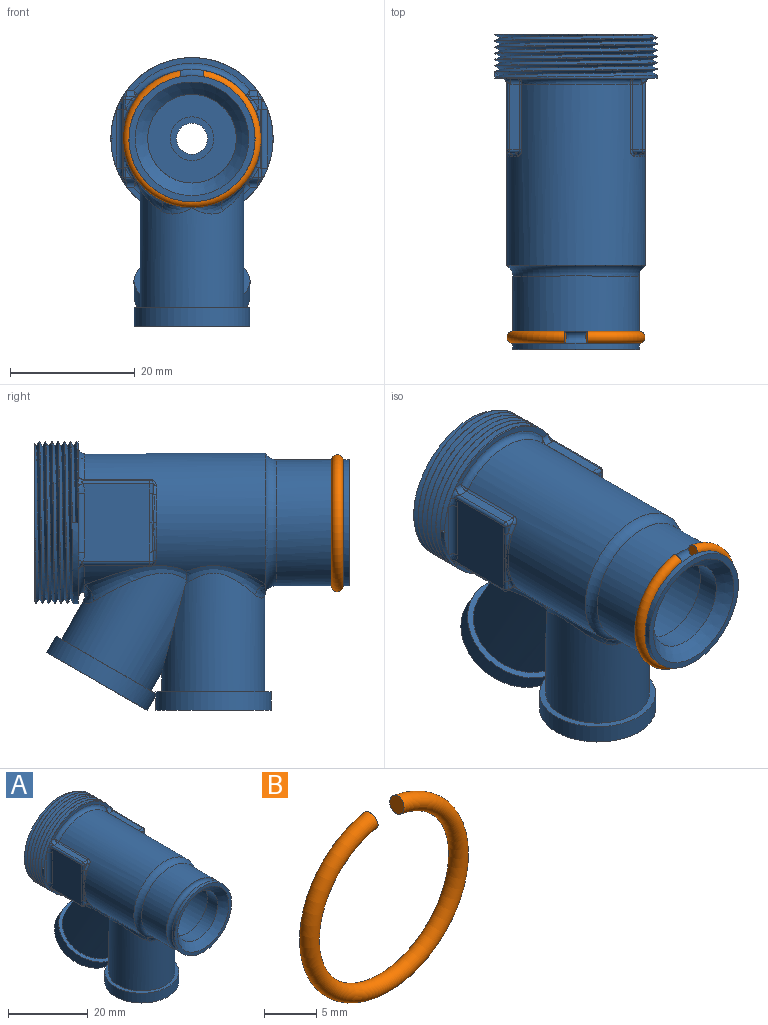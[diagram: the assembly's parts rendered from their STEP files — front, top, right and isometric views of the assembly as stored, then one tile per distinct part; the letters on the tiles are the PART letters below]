
ASSEMBLY  parts=2 mates=1
PART A: 126 faces, bbox 27.1x52x45.9 mm
  f0: cylinder r=10.11mm len=20.22mm, axis (0,1,0), area 60.1mm2, adj f90,f115
  f1: cylinder r=10.11mm len=20.22mm, axis (0,1,0), area 560.4mm2, adj f115,f121
  f2: cylinder r=9.5mm len=20.4mm, axis (0,1,0), area 1205mm2, adj f103,f105,f106
  f3: cylinder r=9.5mm len=22mm, axis (0,1,0), area 1298.6mm2, adj f104,f107,f125
  f4: cylinder r=7.11mm len=14.22mm, axis (0,-1,0), area 160.8mm2, adj f103,f124
  f5: cylinder r=9.3mm len=18.6mm, axis (0,0,-1), area 174.8mm2, adj f92,f93,f99,f101
  f6: cylinder r=11.11mm len=29mm, axis (0,1,0), area 1173.3mm2, adj f29,f30,f31,f34,f36,f42,f44,f45
  f7: plane 20.87x5.25mm, normal (0,-1,0), area 20.2mm2, adj f14,f85,f86,f89
  f8: plane 9.45x0.89mm, normal (0,-1,0), area 5.6mm2, adj f14,f78
  f9: plane 9.45x0.89mm, normal (0,-1,0), area 5.6mm2, adj f14,f77
  f10: plane 1.54x0.83mm, normal (0,-1,0), area 0.6mm2, adj f38,f42,f43
  f11: plane 1.54x0.83mm, normal (0,-1,0), area 0.6mm2, adj f32,f36,f37
  f12: plane 1.54x0.83mm, normal (0,-1,0), area 0.6mm2, adj f58,f62,f65
  f13: plane 20.87x5.25mm, normal (0,-1,0), area 20.2mm2, adj f14,f66,f69,f70
  f14: cylinder r=13mm len=26mm, axis (0,1,0), area 72.4mm2, adj f7,f8,f9,f13,f15,f23,f24,f25
  f15: plane 26.07x26.07mm, normal (0,1,0), area 84.2mm2, adj f14,f23,f24,f125
  f16: plane 10.51x1.54mm, normal (0,0,1), area 16.2mm2, adj f54,f61,f62,f83,f85
  f17: plane 10.51x1.54mm, normal (0,0,1), area 16.2mm2, adj f39,f43,f45,f84,f86
  f18: plane 12.5x10.72mm, normal (-1,0,0), area 131.5mm2, adj f26,f27,f33,f37,f38,f39,f76,f78
  f19: plane 10.51x1.54mm, normal (0,0,-1), area 16.2mm2, adj f31,f32,f33,f70,f72
  f20: plane 10.51x1.54mm, normal (0,0,-1), area 16.2mm2, adj f51,f52,f53,f69,f71
  f21: plane 12.5x10.72mm, normal (1,0,0), area 131.5mm2, adj f48,f49,f51,f54,f58,f59,f75,f77
  f22: plane 1.54x0.83mm, normal (0,-1,0), area 0.6mm2, adj f52,f59,f60
  f23: bspline ~30.02x26mm, area 475.4mm2, adj f14,f15,f24,f25
  f24: bspline ~30.02x26mm, area 508mm2, adj f14,f15,f23,f25
  f25: plane 0.95x0.82mm, normal (0,0,1), area 0.4mm2, adj f14,f23,f24
  f26: bspline ~4.71x0.5mm, area 2mm2, adj f18,f27,f38,f40
  f27: bspline ~4.71x0.5mm, area 2mm2, adj f18,f26,f28,f37
  f28: bspline ~4.71x0.81mm, area 1.5mm2, adj f27,f29,f36,f37
  f29: bspline ~4.54x0.96mm, area 1.7mm2, adj f6,f28,f30,f36
  f30: bspline ~4.54x0.96mm, area 1.7mm2, adj f6,f29,f40,f42
  f31: cylinder r=0.5mm len=10.5mm, axis (0,1,0), area 4.7mm2, adj f6,f19,f34,f68
  f32: cylinder r=0.5mm len=1.54mm, axis (-1,0,0), area 0.9mm2, adj f11,f19,f34,f35
  f33: cylinder r=0.5mm len=10.91mm, axis (0,1,0), area 8.4mm2, adj f18,f19,f35,f74
  f34: bspline ~1.28x1.23mm, area 0.8mm2, adj f6,f31,f32,f36
  f35: sphere r=0.5mm, area 0.4mm2, adj f32,f33,f37
  f36: torus R=11.61mm, axis (0,-1,0), area 1.4mm2, adj f6,f11,f28,f29,f34
  f37: cylinder r=0.5mm len=1.57mm, axis (0,0,1), area 1.2mm2, adj f11,f18,f27,f28,f35
  f38: cylinder r=0.5mm len=1.57mm, axis (0,0,1), area 1.2mm2, adj f10,f18,f26,f40,f41
  f39: cylinder r=0.5mm len=10.91mm, axis (0,1,0), area 8.4mm2, adj f17,f18,f41,f82
  f40: bspline ~4.71x0.81mm, area 1.5mm2, adj f26,f30,f38,f42
  f41: sphere r=0.5mm, area 0.4mm2, adj f38,f39,f43
  f42: torus R=11.61mm, axis (0,-1,0), area 1.4mm2, adj f6,f10,f30,f40,f44
  f43: cylinder r=0.5mm len=1.54mm, axis (1,0,0), area 0.9mm2, adj f10,f17,f41,f44
  f44: bspline ~1.25x1.19mm, area 0.8mm2, adj f6,f42,f43,f45
  f45: cylinder r=0.5mm len=10.5mm, axis (0,1,0), area 4.7mm2, adj f6,f17,f44,f88
  f46: bspline ~4.54x0.96mm, area 1.7mm2, adj f6,f47,f60,f63
  f47: bspline ~4.71x0.81mm, area 1.5mm2, adj f46,f48,f59,f60
  f48: bspline ~4.71x0.5mm, area 2mm2, adj f21,f47,f49,f59
  f49: bspline ~4.71x0.5mm, area 2mm2, adj f21,f48,f50,f58
  f50: bspline ~4.71x0.81mm, area 1.5mm2, adj f49,f58,f63,f65
  f51: cylinder r=0.5mm len=10.91mm, axis (0,1,0), area 8.4mm2, adj f20,f21,f55,f73
  f52: cylinder r=0.5mm len=1.54mm, axis (-1,0,0), area 0.9mm2, adj f20,f22,f55,f56
  f53: cylinder r=0.5mm len=10.5mm, axis (0,1,0), area 4.7mm2, adj f6,f20,f56,f67
  f54: cylinder r=0.5mm len=10.91mm, axis (0,1,0), area 8.4mm2, adj f16,f21,f57,f81
  f55: sphere r=0.5mm, area 0.4mm2, adj f51,f52,f59
  f56: bspline ~1.25x1.19mm, area 0.8mm2, adj f6,f52,f53,f60
  f57: sphere r=0.5mm, area 0.4mm2, adj f54,f58,f62
  f58: cylinder r=0.5mm len=1.57mm, axis (0,0,-1), area 1.2mm2, adj f12,f21,f49,f50,f57
  f59: cylinder r=0.5mm len=1.57mm, axis (0,0,-1), area 1.2mm2, adj f21,f22,f47,f48,f55
  f60: torus R=11.61mm, axis (0,-1,0), area 1.4mm2, adj f6,f22,f46,f47,f56
  f61: cylinder r=0.5mm len=10.5mm, axis (0,1,0), area 4.7mm2, adj f6,f16,f64,f87
  f62: cylinder r=0.5mm len=1.54mm, axis (1,0,0), area 0.9mm2, adj f12,f16,f57,f64
  f63: bspline ~4.54x0.96mm, area 1.7mm2, adj f6,f46,f50,f65
  f64: bspline ~1.28x1.23mm, area 0.8mm2, adj f6,f61,f62,f65
  f65: torus R=11.61mm, axis (0,-1,0), area 1.4mm2, adj f6,f12,f50,f63,f64
  f66: torus R=12.11mm, axis (0,-1,0), area 31.9mm2, adj f6,f13,f67,f68,f118
  f67: bspline ~1.23x1mm, area 0.3mm2, adj f53,f66,f69
  f68: bspline ~1.23x1mm, area 0.3mm2, adj f31,f66,f70
  f69: cylinder r=1mm len=1.37mm, axis (1,0,0), area 2mm2, adj f13,f20,f67,f71
  f70: cylinder r=1mm len=1.37mm, axis (1,0,0), area 2mm2, adj f13,f19,f68,f72
  f71: bspline ~1.11x1.11mm, area 0.2mm2, adj f14,f20,f69,f73
  f72: bspline ~1.14x1.14mm, area 0.2mm2, adj f14,f19,f70,f74
  f73: bspline ~1.89x1.16mm, area 1.1mm2, adj f14,f51,f71,f75
  f74: bspline ~1.82x1.12mm, area 1.1mm2, adj f14,f33,f72,f76
  f75: bspline ~2.1x1.1mm, area 1.8mm2, adj f14,f21,f73,f77
  f76: bspline ~1.52x1mm, area 1.7mm2, adj f14,f18,f74,f78
  f77: cylinder r=1mm len=9.45mm, axis (0,0,1), area 14.8mm2, adj f9,f21,f75,f79
  f78: cylinder r=1mm len=9.45mm, axis (0,0,-1), area 14.8mm2, adj f8,f18,f76,f80
  f79: bspline ~1.52x1mm, area 1.7mm2, adj f14,f21,f77,f81
  f80: bspline ~2.1x1.1mm, area 1.8mm2, adj f14,f18,f78,f82
  f81: bspline ~1.82x1.12mm, area 1.1mm2, adj f14,f54,f79,f83
  f82: bspline ~1.89x1.16mm, area 1.1mm2, adj f14,f39,f80,f84
  f83: bspline ~1.14x1.14mm, area 0.2mm2, adj f14,f16,f81,f85
  f84: bspline ~1.11x1.11mm, area 0.2mm2, adj f14,f17,f82,f86
  f85: cylinder r=1mm len=1.37mm, axis (-1,0,0), area 2mm2, adj f7,f16,f83,f87
  f86: cylinder r=1mm len=1.37mm, axis (-1,0,0), area 2mm2, adj f7,f17,f84,f88
  f87: bspline ~1.23x1mm, area 0.3mm2, adj f61,f85,f89
  f88: bspline ~1.23x1mm, area 0.3mm2, adj f45,f86,f89
  f89: torus R=12.11mm, axis (0,-1,0), area 31.9mm2, adj f6,f7,f87,f88
  f90: plane 20.22x20.22mm, normal (0,-1,0), area 60.4mm2, adj f0,f124
  f91: cylinder r=8.3mm len=18.97mm, axis (0,0,-1), area 744.6mm2, adj f92,f102,f117,f119,f122,f123
  f92: plane 18.6x18.6mm, normal (0,0,1), area 55.3mm2, adj f5,f91
  f93: plane 18.6x18.6mm, normal (0,0,-1), area 183.5mm2, adj f5,f94
  f94: cylinder r=5.3mm len=10.6mm, axis (0,0,-1), area 299.7mm2, adj f93,f95
  f95: plane 10.6x10.6mm, normal (0,0,-1), area 75.7mm2, adj f94,f105
  f96: cone r=5.51mm half-angle=1.8deg, axis (0,-0.5,0.87), area 237.4mm2, adj f97,f100
  f97: cylinder r=5.3mm len=10.95mm, axis (0,0.5,-0.87), area 117.6mm2, adj f96,f98
  f98: plane 18.6x16.11mm, normal (0,0.5,-0.87), area 183.5mm2, adj f97,f101
  f99: plane 18.63x16.06mm, normal (0,-0.5,0.87), area 55mm2, adj f5,f101,f102
  f100: plane 11.03x9.55mm, normal (0,0.5,-0.87), area 82.9mm2, adj f96,f104
  f101: cylinder r=9.3mm len=18.6mm, axis (0,0.5,-0.87), area 174.9mm2, adj f5,f98,f99
  f102: cylinder r=8.3mm len=24.11mm, axis (0,0.5,-0.87), area 581.4mm2, adj f91,f99,f116,f117,f118,f120,f122
  f103: plane 19x19mm, normal (0,1,0), area 124.7mm2, adj f2,f4
  f104: cylinder r=2mm len=9.83mm, axis (0,0.5,-0.87), area 99.1mm2, adj f3,f100
  f105: cylinder r=2mm len=11.59mm, axis (0,0,-1), area 145.6mm2, adj f2,f95
  f106: plane 19x19mm, normal (0,-1,0), area 245mm2, adj f2,f114
  f107: plane 19x19mm, normal (0,1,0), area 219.9mm2, adj f3,f108
  f108: cylinder r=4.5mm len=9mm, axis (0,1,0), area 42.4mm2, adj f107,f109
  f109: plane 9x9mm, normal (0,1,0), area 25.1mm2, adj f108,f110
  f110: cylinder r=3.5mm len=7mm, axis (0,1,0), area 66mm2, adj f109,f111
  f111: plane 7x7mm, normal (0,1,0), area 18.8mm2, adj f110,f112
  f112: cylinder r=2.5mm len=7.54mm, axis (0,1,0), area 118.4mm2, adj f111,f113
  f113: plane 7x7mm, normal (0,-1,0), area 18.8mm2, adj f112,f114
  f114: cylinder r=3.5mm len=7mm, axis (0,1,0), area 55.8mm2, adj f106,f113
  f115: torus R=10.11mm, axis (0,-1,0), area 186.8mm2, adj f0,f1
  f116: bspline ~18.63x6.26mm, area 34.6mm2, adj f6,f102,f117,f118
  f117: bspline ~15.29x5.22mm, area 24.1mm2, adj f6,f91,f102,f116,f119
  f118: bspline ~9.98x3.05mm, area 20.8mm2, adj f66,f102,f116,f120
  f119: bspline ~5.52x2.44mm, area 4.2mm2, adj f91,f117,f121
  f120: bspline ~18.11x5.93mm, area 34.6mm2, adj f6,f102,f118,f122
  f121: torus R=12.11mm, axis (0,1,0), area 137.6mm2, adj f1,f6,f119,f123
  f122: bspline ~15.29x5.22mm, area 24.1mm2, adj f6,f91,f102,f120,f123
  f123: bspline ~5.52x2.44mm, area 4.2mm2, adj f91,f121,f122
  f124: cone r=7.11mm half-angle=45deg, axis (0,-1,0), area 144.1mm2, adj f4,f90
  f125: cone r=11.5mm half-angle=45deg, axis (0,1,0), area 186.6mm2, adj f3,f15
PART B: 3 faces, bbox 23.9x1.9x23.8 mm
  f0: torus R=10.11mm, axis (0,1,0), area 358.2mm2, adj f1,f2
  f1: plane 1.9x1.87mm, normal (0.98,0,0.17), area 2.8mm2, adj f0
  f2: plane 1.9x1.87mm, normal (-0.98,0,0.17), area 2.8mm2, adj f0
PLACE A t=(-41.35,5.55,-49.13)mm
PLACE B t=(-41.35,5.55,-49.13)mm
MATE fastened B.f0 <-> A.f0  axis (0,1,0) through (-41.35,-43,-49.13)mm
